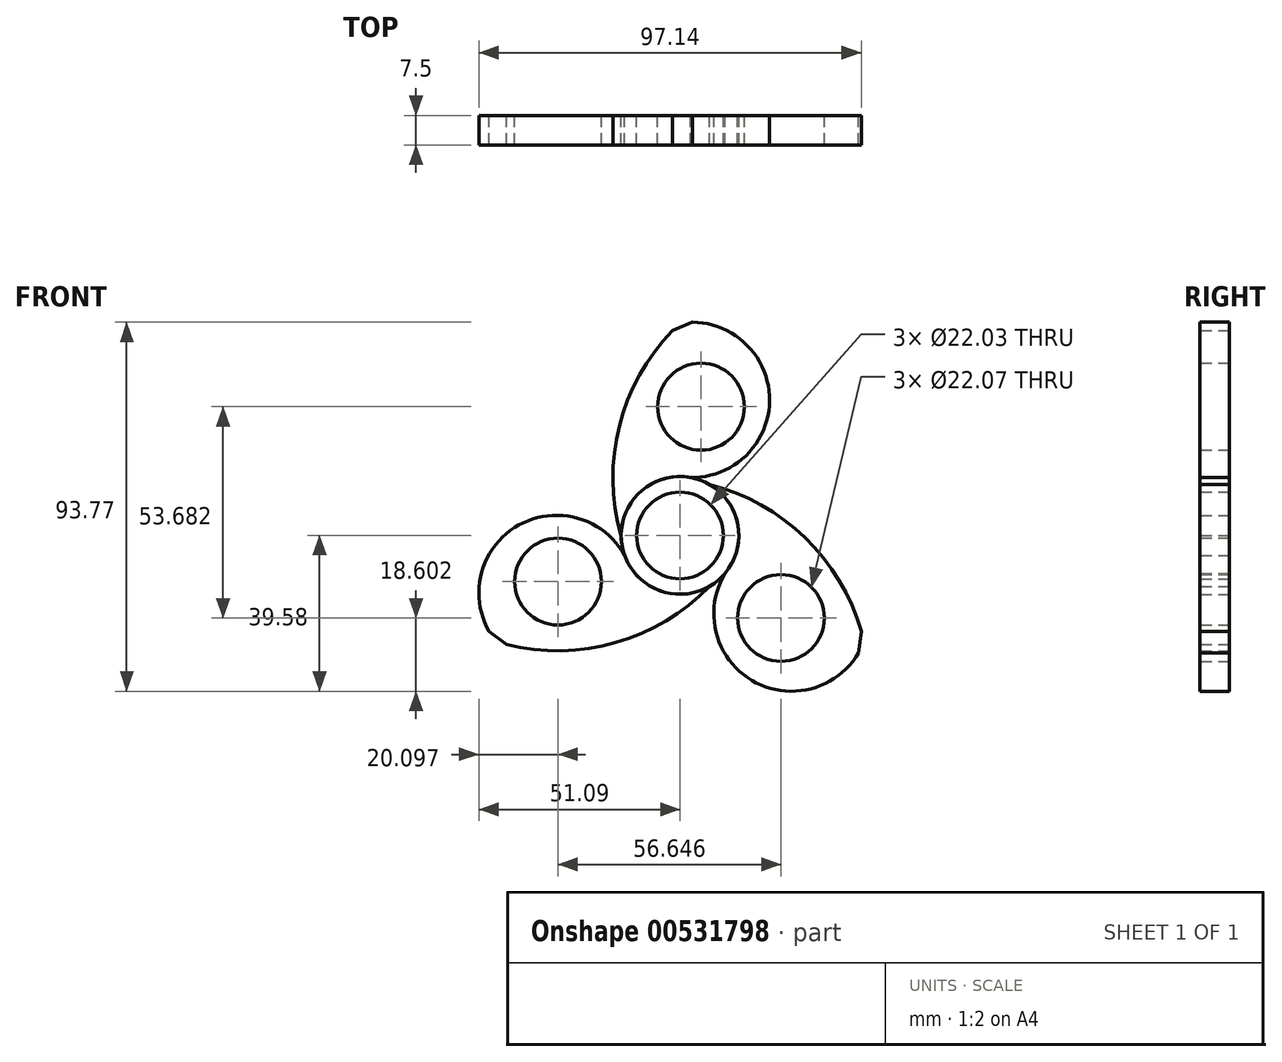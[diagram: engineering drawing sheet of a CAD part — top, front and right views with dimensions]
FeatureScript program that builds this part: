
annotation { "Feature Type Name" : "Feature", "Feature Type Description" : "" }
export const myFeature = defineFeature(function(context is Context, id is Id, definition is map)
    precondition{}
    {
        {
            var Q0;
            Q0=qCreatedBy(makeId("Front.planeOp"),FACE);
            var sketch = newSketch(context, id + "F0", { "sketchPlane" : qUnion([Q0])});
            skCircle(sketch, "E0", {"center": v(0, 0) * mm, "radius": 11.01 * mm});
            skCircle(sketch, "E1", {"center": v(0, 0) * mm, "radius": 14.95 * mm});
            skArc(sketch, "E2", {"start": v(0, 53.95) * mm, "mid": v(-15.08, 29.08) * mm, "end": v(-14.95, 0) * mm});
            skArc(sketch, "E3", {"start": v(0, 14.95) * mm, "mid": v(22.76, 34.45) * mm, "end": v(0, 53.95) * mm});
            skCircle(sketch, "E4", {"center": v(5.34, 32.7) * mm, "radius": 11.04 * mm});
            skSolve(sketch);
        }
        {
            var Q0;
            Q0 = qSketchRegion(id + "F0", true);
            extrude(context, id + "F1", {"entities" : qUnion([Q0]), "depth" : 7.5 * mm, "offsetDistance" : 25 * mm});
        }
        {
            var Q0;
            Q0=makeQuery(id+"F1.opExtrude","SWEPT_BODY",BODY,{"disambiguationData":[OSD([sQuery(id+"F0.wireOp",EDGE,"E0"),sQuery(id+"F0.wireOp",EDGE,"E1"),sQuery(id+"F0.wireOp",EDGE,"E2"),sQuery(id+"F0.wireOp",EDGE,"E3"),sQuery(id+"F0.wireOp",EDGE,"E4")])]});
            var Q1;
            Q1=makeQuery(id+"F1.opExtrude","CAP_EDGE",EDGE,{"disambiguationData":[OSD([sQuery(id+"F0.wireOp",EDGE,"E0")])],"isStart":false});
            transform(context, id + "F2", {"entities" : qUnion([Q0]), "transformType" : TransformType.ROTATION, "transformAxis" : qUnion([Q1]), "angle" : 120 * degree, "makeCopy" : true});
        }
        {
            var Q0;
            Q0=makeQuery(id+"F2.opPattern","COPY",BODY,{"derivedFrom":makeQuery(id+"F1.opExtrude","SWEPT_BODY",BODY,{"disambiguationData":[OSD([sQuery(id+"F0.wireOp",EDGE,"E0"),sQuery(id+"F0.wireOp",EDGE,"E1"),sQuery(id+"F0.wireOp",EDGE,"E2"),sQuery(id+"F0.wireOp",EDGE,"E3"),sQuery(id+"F0.wireOp",EDGE,"E4")])]}),"instanceName":"1"});
            var Q1;
            Q1=makeQuery(id+"F1.opExtrude","CAP_EDGE",EDGE,{"disambiguationData":[OSD([sQuery(id+"F0.wireOp",EDGE,"E0")])],"isStart":false});
            transform(context, id + "F3", {"entities" : qUnion([Q0]), "transformType" : TransformType.ROTATION, "transformAxis" : qUnion([Q1]), "angle" : 120 * degree, "makeCopy" : true});
        }
        {
            var Q0;
            Q0=makeQuery(id+"F1.opExtrude","SWEPT_EDGE",EDGE,{"disambiguationData":[OSD([sQuery(id+"F0.wireOp",EDGE,"E2"),sQuery(id+"F0.wireOp",EDGE,"E3")])]});
            var Q1;
            Q1=makeQuery(id+"F3.opPattern","COPY",EDGE,{"derivedFrom":makeQuery(id+"F2.opPattern","COPY",EDGE,{"derivedFrom":makeQuery(id+"F1.opExtrude","SWEPT_EDGE",EDGE,{"disambiguationData":[OSD([sQuery(id+"F0.wireOp",EDGE,"E2"),sQuery(id+"F0.wireOp",EDGE,"E3")])]}),"instanceName":"1"}),"instanceName":"1"});
            var Q2;
            Q2=makeQuery(id+"F2.opPattern","COPY",EDGE,{"derivedFrom":makeQuery(id+"F1.opExtrude","SWEPT_EDGE",EDGE,{"disambiguationData":[OSD([sQuery(id+"F0.wireOp",EDGE,"E2"),sQuery(id+"F0.wireOp",EDGE,"E3")])]}),"instanceName":"1"});
            chamfer(context, id + "F4", {"entities" : qUnion([Q0, Q1, Q2]), "width" : 7 * mm, "tangentPropagation" : true});
        }
    });
